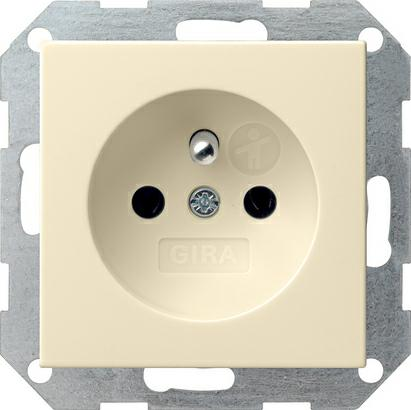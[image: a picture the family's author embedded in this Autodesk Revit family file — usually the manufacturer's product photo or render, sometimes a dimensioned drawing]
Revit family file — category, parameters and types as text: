
# Revit family: E_Cable Junction Box_MEPcontent_Spelsberg_BS 2_INT-EN
name_source: partatom
category: Electrical Fixtures
revit_build: Autodesk Revit 2017 (Build: 20160225_1515(x64)
units: mm (PartAtom-declared; Revit-internal decimal feet)

## family parameters
Always vertical = Yes
Cut with Voids When Loaded = No
Maintain Annotation Orientation = Yes
OmniClass Number = 23.80.30.14.24
OmniClass Title = Junction Boxes
Part Type = Junction Box
Room Calculation Point = No
Round Connector Dimension = Use Diameter
Shared = No
Work Plane-Based = No

## types (1)
- BS 2
    3D Representation = 3DGeometry
    Article Description = Equipment installation box BS 2
    Article Type = BS 2
    Blue = Color RAL 5013
    Description = Equipment installation box BS 2
    ETIM Article Class = EC002601
    Green = Color RAL 6018
    Height = 59.1 mm  [stored 0.193898 ft]
    IFCExportAs = IfcJunctionBox
    IFCExportType = NOTDEFINED
    Length = 146 mm  [stored 0.479003 ft]
    Manufacturer = Spelsberg
    Manufacturer Art. No. = 97400201
    Manufacturer URL = http://www.spelsberg.com
    Model = BS 2
    Placeholder Height = 59.1 mm  [stored 0.193898 ft]
    Product Line = Spelsberg
    Revit Version = 2017
    Rotation U-Axis Correction = 0.00°
    Rotation U-Axis Default Correction = 0.00°
    Rotation V-Axis Correction = 0.00°
    Rotation V-Axis Default Correction = 0.00°
    Rotation W-Axis Correction = 0.00°
    Rotation W-Axis Default Correction = 0.00°
    Voltage = 230 V
    Width = 86 mm  [stored 0.282152 ft]

note: [stored X ft] marks values corroborated as IEEE doubles in the binary element streams (Revit-internal decimal feet)

## geometry (parser evidence)
native form markers: Sweep x15
no freeform markers — native parametric forms only
